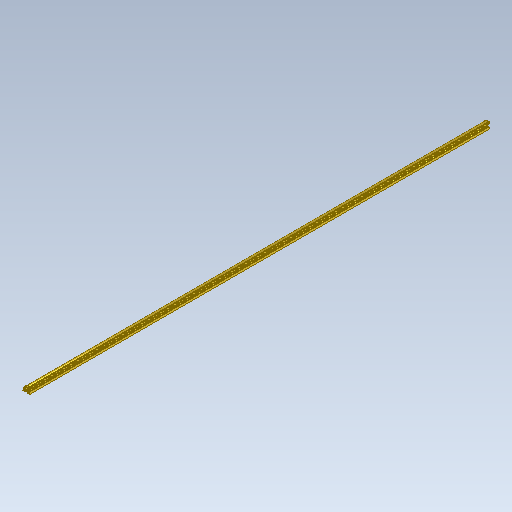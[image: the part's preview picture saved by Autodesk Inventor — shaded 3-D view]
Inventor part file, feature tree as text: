
AUTODESK INVENTOR PART (.ipt)
format: ipt  version: 2025.2 (Build 292293000, 293)  size: 304,640 bytes
history: native  units: mm
features: other x1, extrude x1, mirror x1, sketch x1
ambient origin geometry x8: Origin, YZ Plane, XZ Plane, XY Plane, X Axis, Y Axis, Z Axis, Center Point
bodies: Body1 (feature_tree)
feature tree (4):
  other  "Sólido1"
  extrude  "Extrusão1"  Depth=2000.0mm
  mirror  "Espelhar1"
  sketch  "Esboço1"  dims[d0=10.0mm d1=30.0mm d2=15.0mm d3=8.0mm d4=8.2mm d10=11.5mm d11=5.0mm d12=1.1mm d13=1.1mm d14=1.1mm d15=2.2mm d16=1.25mm d19=1.0mm d20=7.396555mm d25=2.0mm d27=2000.0mm d28=0.0mm]
